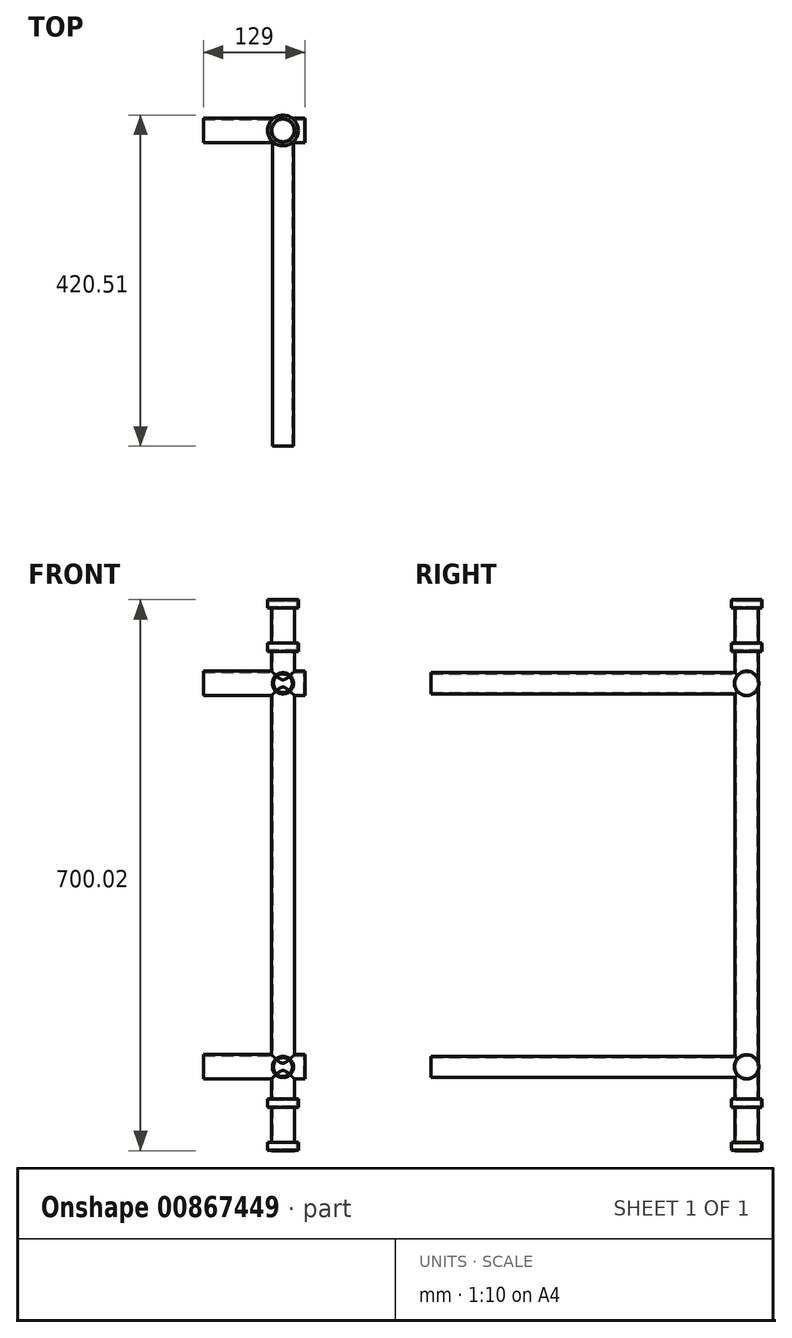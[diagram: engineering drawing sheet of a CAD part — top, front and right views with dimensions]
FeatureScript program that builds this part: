
annotation { "Feature Type Name" : "Feature", "Feature Type Description" : "" }
export const myFeature = defineFeature(function(context is Context, id is Id, definition is map)
    precondition{}
    {
        {
            var Q0;
            Q0=qCreatedBy(makeId("Top.planeOp"),FACE);
            var sketch = newSketch(context, id + "F0", { "sketchPlane" : qUnion([Q0])});
            skCircle(sketch, "E0", {"center": v(0, 0) * mm, "radius": 14.78 * mm});
            skCircle(sketch, "E1", {"center": v(0, 0) * mm, "radius": 19.5 * mm});
            skSolve(sketch);
        }
        {
            var Q0;
            Q0=makeQuery(id+"F0.imprint","IMPRINT",FACE,{"disambiguationData":[TD([[makeQuery(id+"F0.imprint","IMPRINT",EDGE,{"derivedFrom":sQuery(id+"F0.wireOp",EDGE,"E0")}),1.0]])]});
            extrude(context, id + "F1", {"entities" : qUnion([Q0]), "endBound" : BoundingType.SYMMETRIC, "depth" : 700 * mm, "offsetDistance" : 25 * mm});
        }
        {
            var Q0;
            Q0=qCreatedBy(makeId("Front.planeOp"),FACE);
            var sketch = newSketch(context, id + "F2", { "sketchPlane" : qUnion([Q0])});
            skLineSegment(sketch, "E2", {"start": v(0, 350.01) * mm, "end": v(0, 339.15) * mm});
            skLineSegment(sketch, "E3", {"start": v(0, 339.15) * mm, "end": v(19.51, 339.15) * mm});
            skLineSegment(sketch, "E4", {"start": v(19.51, 339.15) * mm, "end": v(19.51, 349.9) * mm});
            skLineSegment(sketch, "E5", {"start": v(19.51, 349.9) * mm, "end": v(0, 350.01) * mm});
            skLineSegment(sketch, "E6.MirrorCS", {"start": v(0, -339.15) * mm, "end": v(19.51, -339.15) * mm});
            skLineSegment(sketch, "E7.MirrorCS", {"start": v(19.51, -339.15) * mm, "end": v(19.51, -349.9) * mm});
            skLineSegment(sketch, "E8.MirrorCS", {"start": v(19.51, -349.9) * mm, "end": v(0, -350.01) * mm});
            skLineSegment(sketch, "E9.MirrorCS", {"start": v(0, -350.01) * mm, "end": v(0, -339.15) * mm});
            skLineSegment(sketch, "E10", {"start": v(0, 339.15) * mm, "end": v(0, 317.05) * mm});
            skLineSegment(sketch, "E11", {"start": v(0, 317.05) * mm, "end": v(68.26, 317.05) * mm});
            skLineSegment(sketch, "E12.MirrorCS", {"start": v(0, 294.95) * mm, "end": v(19.51, 294.95) * mm});
            skLineSegment(sketch, "E13.MirrorCS", {"start": v(19.51, 294.95) * mm, "end": v(19.51, 284.2) * mm});
            skLineSegment(sketch, "E14.MirrorCS", {"start": v(19.51, 284.2) * mm, "end": v(0, 284.1) * mm});
            skLineSegment(sketch, "E15.MirrorCS", {"start": v(0, 284.1) * mm, "end": v(0, 294.95) * mm});
            skLineSegment(sketch, "E16.MirrorCS", {"start": v(19.51, -284.2) * mm, "end": v(0, -284.1) * mm});
            skLineSegment(sketch, "E17.MirrorCS", {"start": v(19.51, -294.95) * mm, "end": v(19.51, -284.2) * mm});
            skLineSegment(sketch, "E18.MirrorCS", {"start": v(0, -294.95) * mm, "end": v(19.51, -294.95) * mm});
            skLineSegment(sketch, "E19.MirrorCS", {"start": v(0, -284.1) * mm, "end": v(0, -294.95) * mm});
            skSolve(sketch);
        }
        {
            var Q0;
            Q0=makeQuery(id+"F2.imprint","IMPRINT",FACE,{"disambiguationData":[TD([[makeQuery(id+"F2.imprint","IMPRINT",EDGE,{"derivedFrom":sQuery(id+"F2.wireOp",EDGE,"E2")}),1.0]])]});
            var Q1;
            Q1=makeQuery(id+"F2.imprint","IMPRINT",FACE,{"disambiguationData":[TD([[makeQuery(id+"F2.imprint","IMPRINT",EDGE,{"derivedFrom":sQuery(id+"F2.wireOp",EDGE,"E12.MirrorCS")}),-1.0]])]});
            var Q2;
            Q2=makeQuery(id+"F2.imprint","IMPRINT",FACE,{"disambiguationData":[TD([[makeQuery(id+"F2.imprint","IMPRINT",EDGE,{"derivedFrom":sQuery(id+"F2.wireOp",EDGE,"E16.MirrorCS")}),1.0]])]});
            var Q3;
            Q3=makeQuery(id+"F2.imprint","IMPRINT",FACE,{"disambiguationData":[TD([[makeQuery(id+"F2.imprint","IMPRINT",EDGE,{"derivedFrom":sQuery(id+"F2.wireOp",EDGE,"E6.MirrorCS")}),-1.0]])]});
            var Q4;
            Q4=sQuery(id+"F2.wireOp",EDGE,"E10");
            revolve(context, id + "F3", {"operationType" : NewBodyOperationType.ADD, "surfaceOperationType" : NewSurfaceOperationType.NEW, "entities" : qUnion([Q0, Q1, Q2, Q3]), "axis" : qUnion([Q4]), "revolveType" : RevolveType.FULL});
        }
        {
            var Q0;
            Q0=qCreatedBy(makeId("Front.planeOp"),FACE);
            var sketch = newSketch(context, id + "F4", { "sketchPlane" : qUnion([Q0])});
            skLineSegment(sketch, "E20", {"start": v(0, 0) * mm, "end": v(0, 230.3) * mm});
            skLineSegment(sketch, "E21.MirrorCS", {"start": v(0, 0) * mm, "end": v(0, -230.3) * mm});
            skCircle(sketch, "E22", {"center": v(0, 243.75) * mm, "radius": 13.45 * mm});
            skCircle(sketch, "E23.MirrorC", {"center": v(0, -243.75) * mm, "radius": 13.45 * mm});
            skSolve(sketch);
        }
        {
            var Q0;
            Q0 = qSketchRegion(id + "F4", true);
            extrude(context, id + "F5", {"entities" : qUnion([Q0]), "operationType" : NewBodyOperationType.ADD, "depth" : 401 * mm, "offsetDistance" : 25 * mm});
        }
        {
            var Q0;
            Q0=qCreatedBy(makeId("Top.planeOp"),FACE);
            var sketch = newSketch(context, id + "F6", { "sketchPlane" : qUnion([Q0])});
            skCircle(sketch, "E24", {"center": v(0, -456.77) * mm, "radius": 12.77 * mm});
            skSolve(sketch);
        }
        {
            var Q0;
            Q0=qCreatedBy(makeId("Right.planeOp"),FACE);
            var sketch = newSketch(context, id + "F7", { "sketchPlane" : qUnion([Q0])});
            skCircle(sketch, "E25", {"center": v(0, 243.56) * mm, "radius": 15.55 * mm});
            skLineSegment(sketch, "E26", {"start": v(-224.68, 240.95) * mm, "end": v(-224.94, 276.85) * mm});
            skLineSegment(sketch, "E27", {"start": v(0, 243.56) * mm, "end": v(-235.77, 243.56) * mm});
            skCircle(sketch, "E28.MirrorC", {"center": v(-449.37, 240.27) * mm, "radius": 15.55 * mm});
            skCircle(sketch, "E29.MirrorC", {"center": v(0, -243.56) * mm, "radius": 15.55 * mm});
            skCircle(sketch, "E30.MirrorC", {"center": v(-449.37, -240.27) * mm, "radius": 15.55 * mm});
            skSolve(sketch);
        }
        {
            var Q0;
            Q0 = qSketchRegion(id + "F7", true);
            extrude(context, id + "F8", {"entities" : qUnion([Q0]), "operationType" : NewBodyOperationType.ADD, "oppositeDirection" : true, "depth" : 101 * mm, "offsetDistance" : 25 * mm, "hasSecondDirection" : true, "secondDirectionOppositeDirection" : false, "secondDirectionDepth" : 28 * mm});
        }
        {
            var Q0;
            Q0=makeQuery(id+"F6.imprint","IMPRINT",FACE,{"disambiguationData":[TD([[makeQuery(id+"F6.imprint","IMPRINT",EDGE,{"derivedFrom":sQuery(id+"F6.wireOp",EDGE,"E24")}),1.0]])]});
            extrude(context, id + "F9", {"entities" : qUnion([Q0]), "endBound" : BoundingType.SYMMETRIC, "depth" : 494 * mm, "offsetDistance" : 25 * mm});
        }
        {
            var Q0;
            Q0=makeQuery(id+"F8.opExtrude","SWEPT_BODY",BODY,{"disambiguationData":[OSD([sQuery(id+"F7.wireOp",EDGE,"E30.MirrorC")])]});
            var Q1;
            Q1=makeQuery(id+"F9.opExtrude","SWEPT_BODY",BODY,{"disambiguationData":[OSD([sQuery(id+"F6.wireOp",EDGE,"E24")])]});
            deleteBodies(context, id + "F10", {"entities" : qUnion([Q0, Q1])});
        }
        {
            var Q0;
            Q0=makeQuery(id+"F8.opExtrude","SWEPT_BODY",BODY,{"disambiguationData":[OSD([sQuery(id+"F7.wireOp",EDGE,"E28.MirrorC")])]});
            deleteBodies(context, id + "F11", {"entities" : qUnion([Q0])});
        }
        {
            var Q0;
            Q0=makeQuery(id+"F5.opExtrude","CAP_FACE",FACE,{"disambiguationData":[OSD([sQuery(id+"F4.wireOp",EDGE,"E23.MirrorC")])],"isStart":false});
            var Q1;
            Q1=makeQuery(id+"F5.opExtrude","CAP_FACE",FACE,{"disambiguationData":[OSD([sQuery(id+"F4.wireOp",EDGE,"E22")])],"isStart":false});
            var Q2;
            Q2=makeQuery(id+"F8.opExtrude","CAP_FACE",FACE,{"disambiguationData":[OSD([sQuery(id+"F7.wireOp",EDGE,"E25")])],"isStart":false});
            var Q3;
            Q3=makeQuery(id+"F8.opExtrude","CAP_FACE",FACE,{"disambiguationData":[OSD([sQuery(id+"F7.wireOp",EDGE,"E29.MirrorC")])],"isStart":false});
            shell(context, id + "F12", {"entities" : qUnion([Q0, Q1, Q2, Q3]), "thickness" : 1.5 * mm});
        }
    });
